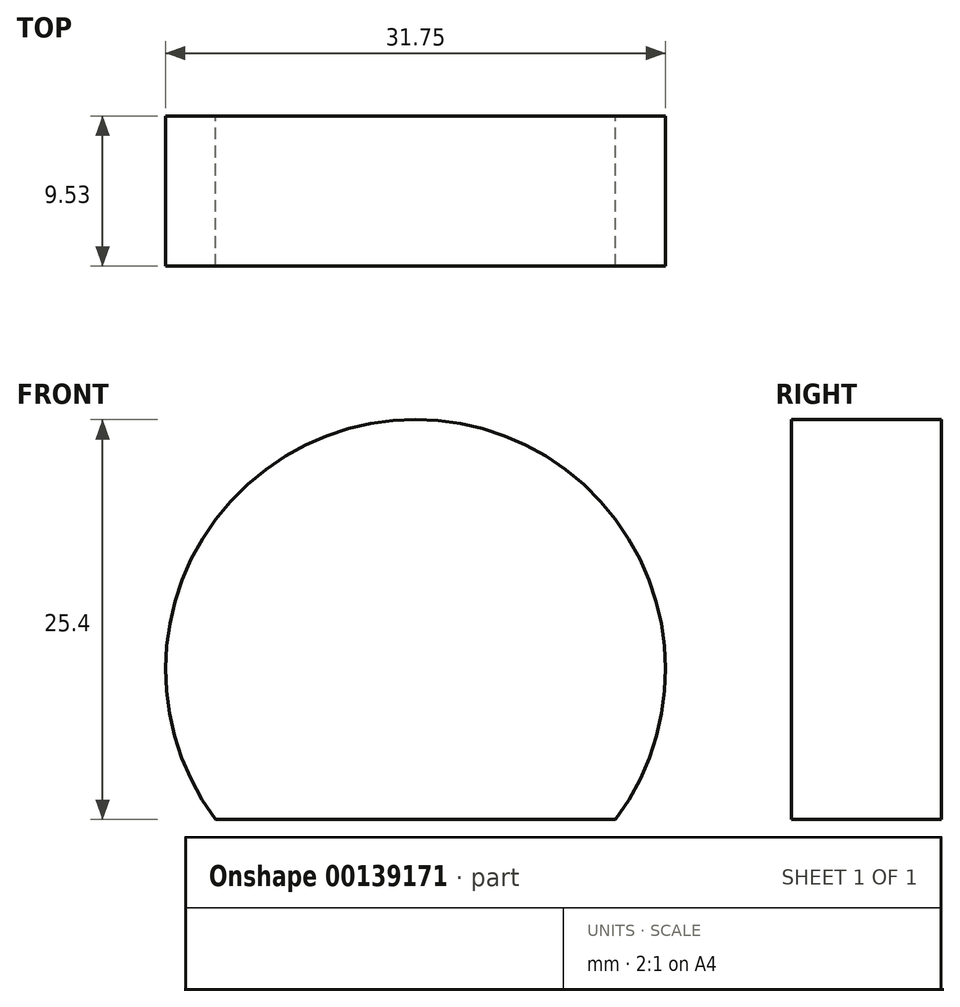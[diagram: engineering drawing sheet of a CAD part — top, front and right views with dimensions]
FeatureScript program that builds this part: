
annotation { "Feature Type Name" : "Feature", "Feature Type Description" : "" }
export const myFeature = defineFeature(function(context is Context, id is Id, definition is map)
    precondition{}
    {
        {
            var Q0;
            Q0=qCreatedBy(makeId("Front.planeOp"),FACE);
            var sketch = newSketch(context, id + "F0", { "sketchPlane" : qUnion([Q0])});
            skLineSegment(sketch, "E0", {"start": v(0, 0) * mm, "end": v(25.4, 0) * mm});
            skArc(sketch, "E1", {"start": v(25.4, 0) * mm, "mid": v(12.7, 25.4) * mm, "end": v(0, 0) * mm});
            skSolve(sketch);
        }
        {
            var Q0;
            Q0 = qSketchRegion(id + "F0", true);
            extrude(context, id + "F1", {"entities" : qUnion([Q0]), "depth" : 9.52 * mm});
        }
    });
